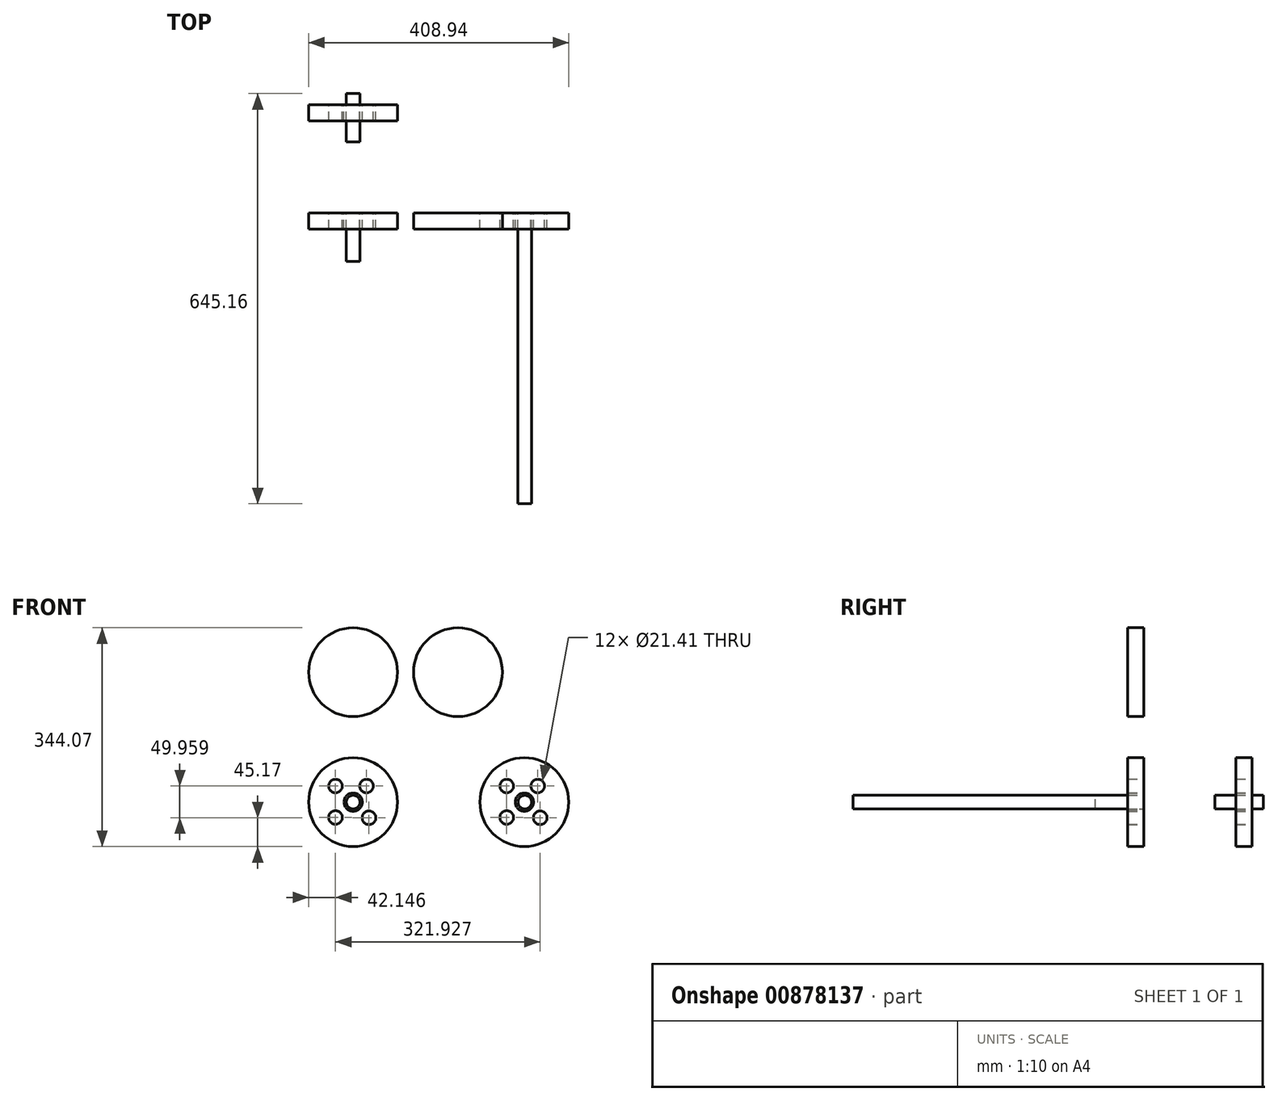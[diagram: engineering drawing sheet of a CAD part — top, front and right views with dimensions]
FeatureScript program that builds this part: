
annotation { "Feature Type Name" : "Feature", "Feature Type Description" : "" }
export const myFeature = defineFeature(function(context is Context, id is Id, definition is map)
    precondition{}
    {
        {
            var Q0;
            Q0=qCreatedBy(makeId("Front.planeOp"),FACE);
            var sketch = newSketch(context, id + "F0", { "sketchPlane" : qUnion([Q0])});
            skCircle(sketch, "E0", {"center": v(0, 0) * mm, "radius": 69.85 * mm});
            skCircle(sketch, "E1", {"center": v(-27.7, 25.28) * mm, "radius": 10.7 * mm});
            skCircle(sketch, "E2", {"center": v(-27.7, -24.09) * mm, "radius": 10.7 * mm});
            skCircle(sketch, "E3", {"center": v(21.05, 25.28) * mm, "radius": 10.7 * mm});
            skCircle(sketch, "E4", {"center": v(24.98, -24.68) * mm, "radius": 10.7 * mm});
            skCircle(sketch, "E5", {"center": v(0, 0) * mm, "radius": 10.7 * mm});
            skCircle(sketch, "E6", {"center": v(0, 0) * mm, "radius": 14.35 * mm});
            skCircle(sketch, "E7", {"center": v(-931.84, -91.32) * mm, "radius": 69.85 * mm});
            skCircle(sketch, "E8", {"center": v(-214.04, 247.96) * mm, "radius": 71.12 * mm});
            skCircle(sketch, "E9", {"center": v(0, 204.37) * mm, "radius": 69.85 * mm});
            skSolve(sketch);
        }
        {
            var Q0;
            Q0=sQuery(id+"F0.wireOp",EDGE,"E1");
            var Q1;
            Q1=sQuery(id+"F0.wireOp",EDGE,"E2");
            var Q2;
            Q2=sQuery(id+"F0.wireOp",EDGE,"E4");
            var Q3;
            Q3=sQuery(id+"F0.wireOp",EDGE,"E6");
            var Q4;
            Q4=sQuery(id+"F0.wireOp",EDGE,"E3");
            extrude(context, id + "F1", {"bodyType" : ToolBodyType.SURFACE, "surfaceEntities" : qUnion([Q0, Q1, Q2, Q3, Q4]), "depth" : 25.4 * mm, "offsetDistance" : 25.4 * mm});
        }
        {
            var Q0;
            Q0=makeQuery(id+"F0.imprint","IMPRINT",FACE,{"disambiguationData":[TD([[makeQuery(id+"F0.imprint","IMPRINT",EDGE,{"derivedFrom":sQuery(id+"F0.wireOp",EDGE,"E0")}),1.0]])]});
            extrude(context, id + "F2", {"entities" : qUnion([Q0]), "depth" : 25.4 * mm, "offsetDistance" : 25.4 * mm});
        }
        {
            var Q0;
            Q0=makeQuery(id+"F0.imprint","IMPRINT",FACE,{"disambiguationData":[TD([[makeQuery(id+"F0.imprint","IMPRINT",EDGE,{"derivedFrom":sQuery(id+"F0.wireOp",EDGE,"E5")}),1.0]])]});
            extrude(context, id + "F3", {"entities" : qUnion([Q0]), "depth" : 76.2 * mm, "offsetDistance" : 25.4 * mm});
        }
        {
            var Q0;
            Q0=sQuery(id+"F0.wireOp",EDGE,"E8");
            extrude(context, id + "F4", {"bodyType" : ToolBodyType.SURFACE, "surfaceEntities" : qUnion([Q0]), "depth" : 436.88 * mm, "offsetDistance" : 25.4 * mm});
        }
        {
            var Q0;
            Q0=makeQuery(id+"F0.imprint","IMPRINT",FACE,{"disambiguationData":[TD([[makeQuery(id+"F0.imprint","IMPRINT",EDGE,{"derivedFrom":sQuery(id+"F0.wireOp",EDGE,"E9")}),1.0]])]});
            extrude(context, id + "F5", {"entities" : qUnion([Q0]), "depth" : 25.4 * mm, "offsetDistance" : 25.4 * mm});
        }
        {
            var Q0;
            Q0=makeQuery(id+"F2.opExtrude","SWEPT_BODY",BODY,{"disambiguationData":[OSD([sQuery(id+"F0.wireOp",EDGE,"E0"),sQuery(id+"F0.wireOp",EDGE,"E1"),sQuery(id+"F0.wireOp",EDGE,"E2"),sQuery(id+"F0.wireOp",EDGE,"E3"),sQuery(id+"F0.wireOp",EDGE,"E4"),sQuery(id+"F0.wireOp",EDGE,"E6")])]});
            transform(context, id + "F6", {"entities" : qUnion([Q0]), "transformType" : TransformType.TRANSLATION_3D, "dx" : 269.24 * mm, "dy" : 0 * mm, "dz" : 0 * mm, "makeCopy" : true});
        }
        {
            var Q0;
            Q0=makeQuery(id+"F3.opExtrude","SWEPT_BODY",BODY,{"disambiguationData":[OSD([sQuery(id+"F0.wireOp",EDGE,"E5")])]});
            transform(context, id + "F7", {"entities" : qUnion([Q0]), "transformType" : TransformType.TRANSLATION_3D, "dx" : 270 * mm, "dy" : 0 * mm, "dz" : 0 * mm, "makeCopy" : true});
        }
        {
            var Q0;
            Q0=makeQuery(id+"F5.opExtrude","SWEPT_BODY",BODY,{"disambiguationData":[OSD([sQuery(id+"F0.wireOp",EDGE,"E9")])]});
            transform(context, id + "F8", {"entities" : qUnion([Q0]), "transformType" : TransformType.TRANSLATION_3D, "dx" : 164.85 * mm, "dy" : 0 * mm, "dz" : 0 * mm, "makeCopy" : true});
        }
        {
            var Q0;
            Q0=makeQuery(id+"F7.opPattern","COPY",FACE,{"derivedFrom":makeQuery(id+"F3.opExtrude","CAP_FACE",FACE,{"disambiguationData":[OSD([sQuery(id+"F0.wireOp",EDGE,"E5")])],"isStart":false}),"instanceName":"1"});
            extrude(context, id + "F9", {"entities" : qUnion([Q0]), "operationType" : NewBodyOperationType.ADD, "depth" : 381 * mm, "offsetDistance" : 25.4 * mm});
        }
        {
            var Q0;
            Q0=makeQuery(id+"F2.opExtrude","SWEPT_BODY",BODY,{"disambiguationData":[OSD([sQuery(id+"F0.wireOp",EDGE,"E0"),sQuery(id+"F0.wireOp",EDGE,"E1"),sQuery(id+"F0.wireOp",EDGE,"E2"),sQuery(id+"F0.wireOp",EDGE,"E3"),sQuery(id+"F0.wireOp",EDGE,"E4"),sQuery(id+"F0.wireOp",EDGE,"E6")])]});
            transform(context, id + "F10", {"entities" : qUnion([Q0]), "transformType" : TransformType.TRANSLATION_3D, "dx" : 0 * mm, "dy" : 170.18 * mm, "dz" : 0 * mm, "makeCopy" : true});
        }
        {
            var Q0;
            Q0=makeQuery(id+"F3.opExtrude","SWEPT_BODY",BODY,{"disambiguationData":[OSD([sQuery(id+"F0.wireOp",EDGE,"E5")])]});
            transform(context, id + "F11", {"entities" : qUnion([Q0]), "transformType" : TransformType.TRANSLATION_3D, "dx" : 0 * mm, "dy" : 187.96 * mm, "dz" : 0 * mm, "makeCopy" : true});
        }
    });
